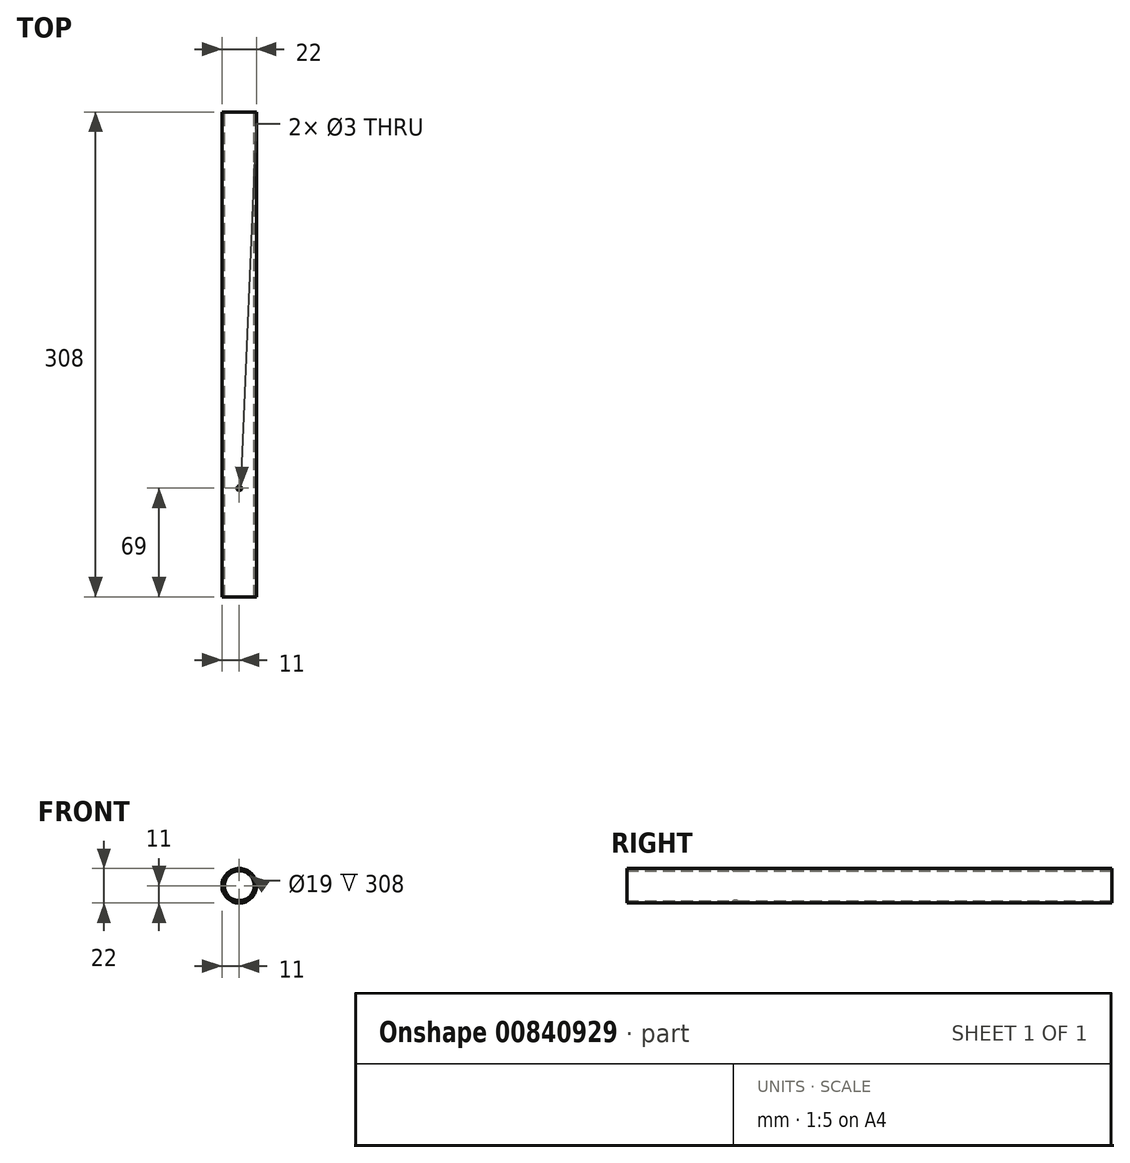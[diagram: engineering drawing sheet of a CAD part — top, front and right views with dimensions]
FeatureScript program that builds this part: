
annotation { "Feature Type Name" : "Feature", "Feature Type Description" : "" }
export const myFeature = defineFeature(function(context is Context, id is Id, definition is map)
    precondition{}
    {
        {
            var Q0;
            Q0=qCreatedBy(makeId("Front.planeOp"),FACE);
            var sketch = newSketch(context, id + "F0", { "sketchPlane" : qUnion([Q0])});
            skCircle(sketch, "E0", {"center": v(0, 0) * mm, "radius": 11 * mm});
            skCircle(sketch, "E1", {"center": v(0, 0) * mm, "radius": 9.5 * mm});
            skSolve(sketch);
        }
        {
            var Q0;
            Q0 = qSketchRegion(id + "F0", true);
            extrude(context, id + "F1", {"entities" : qUnion([Q0]), "endBound" : BoundingType.SYMMETRIC, "depth" : 308 * mm, "offsetDistance" : 25 * mm});
        }
        {
            var Q0;
            Q0=qCreatedBy(makeId("Top.planeOp"),FACE);
            var sketch = newSketch(context, id + "F2", { "sketchPlane" : qUnion([Q0])});
            skCircle(sketch, "E2", {"center": v(0, -85) * mm, "radius": 1.5 * mm});
            skSolve(sketch);
        }
        {
            var Q0;
            Q0 = qSketchRegion(id + "F2", true);
            extrude(context, id + "F3", {"entities" : qUnion([Q0]), "operationType" : NewBodyOperationType.REMOVE, "endBound" : BoundingType.SYMMETRIC, "oppositeDirection" : true, "depth" : 25 * mm, "offsetDistance" : 25 * mm});
        }
    });
